# Revit family: JC KONTAKTER JCK297 SV
name_source: partatom
category: Specialty Equipment
units: mm (PartAtom-declared; Revit-internal decimal feet)

## family parameters
Cut with Voids When Loaded = No
Enable Cutting in Views = Yes
Host = Face
Maintain Annotation Orientation = Yes
Part Type = Normal
Room Calculation Point = No
Round Connector Dimension = Use Diameter
Shared = No

## types (1)
- JCK297
    CE Dokument = https://jckontakter.se
    Default Elevation = 800 mm  [stored 2.62467 ft]
    End Cap = POM Tenac C 4520
    Lins = Akryl
    Lock = Aluminum ENAW 6060 (Svart)
    Lägsta märkström = 1mA/4 V DC
    Låslock = Aluminum ENAW 6060 (Svart)
    Manufacturer = JC Kontakter
    Mellanvägg = POM Tenac C 4520 (Vit)
    Mikrobrytare = Standard NO/NC IP67 (tre ledare)
    Mikrobrytare (lås) = Standard NO IP67 (två ledare)
    Model = JCK297
    Nominell märkström = 12 V Resistive 6A Inductive L/R 5 ms 6A, 24 V Resistive 6A Inductive L/R 5 ms 5A
    Placering av armbågskontakt = https://jckontakter.se
    Power factor = 1
    Produktvikt = 0.396 kg
    Tekniskt produktblad = https://jckontakter.se
    Tillverkningsland = Sverige
    URL = https://jckontakter.se
    Underdel = Aluminum ENAW 6060
    Voltage = 24 V

note: [stored X ft] marks values corroborated as IEEE doubles in the binary element streams (Revit-internal decimal feet)

## geometry (parser evidence)
native form markers: Sweep x6
no freeform markers — native parametric forms only
